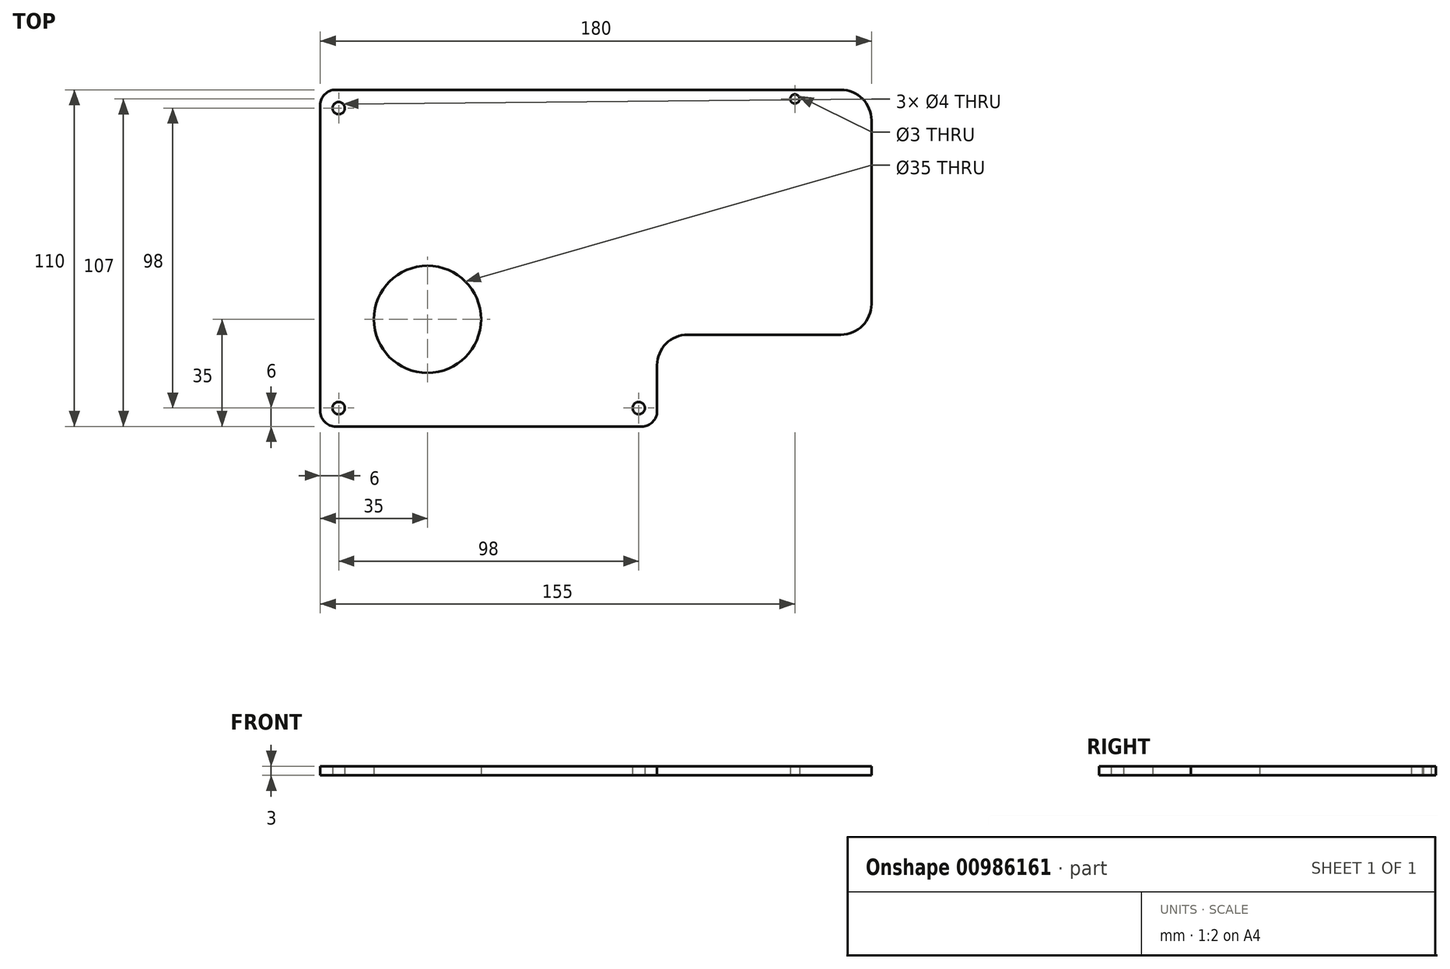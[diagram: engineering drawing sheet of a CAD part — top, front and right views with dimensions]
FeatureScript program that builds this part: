
annotation { "Feature Type Name" : "Feature", "Feature Type Description" : "" }
export const myFeature = defineFeature(function(context is Context, id is Id, definition is map)
    precondition{}
    {
        {
            var Q0;
            Q0=qCreatedBy(makeId("Top.planeOp"),FACE);
            var sketch = newSketch(context, id + "F0", { "sketchPlane" : qUnion([Q0])});
            skLineSegment(sketch, "E0.top", {"start": v(0, 110) * mm, "end": v(180, 110) * mm});
            skLineSegment(sketch, "E0.left", {"start": v(0, 0) * mm, "end": v(0, 110) * mm});
            skLineSegment(sketch, "E1", {"start": v(180, 110) * mm, "end": v(180, 30) * mm});
            skLineSegment(sketch, "E2", {"start": v(180, 30) * mm, "end": v(110, 30) * mm});
            skLineSegment(sketch, "E3", {"start": v(110, 30) * mm, "end": v(110, 0) * mm});
            skLineSegment(sketch, "E4", {"start": v(110, 0) * mm, "end": v(0, 0) * mm});
            skCircle(sketch, "E5", {"center": v(6, 104) * mm, "radius": 2 * mm});
            skCircle(sketch, "E6", {"center": v(6, 6) * mm, "radius": 2 * mm});
            skCircle(sketch, "E7", {"center": v(104, 6) * mm, "radius": 2 * mm});
            skCircle(sketch, "E8", {"center": v(155, 107) * mm, "radius": 1.5 * mm});
            skCircle(sketch, "E9", {"center": v(35, 35) * mm, "radius": 17.5 * mm});
            skSolve(sketch);
        }
        {
            var Q0;
            Q0=makeQuery(id+"F0.imprint","IMPRINT",FACE,{"disambiguationData":[TD([[makeQuery(id+"F0.imprint","IMPRINT",EDGE,{"derivedFrom":sQuery(id+"F0.wireOp",EDGE,"E0.top")}),-1.0]])]});
            extrude(context, id + "F1", {"entities" : qUnion([Q0]), "depth" : 3 * mm, "offsetDistance" : 25 * mm});
        }
        {
            var Q0;
            Q0=makeQuery(id+"F1.opExtrude","SWEPT_EDGE",EDGE,{"disambiguationData":[OSD([sQuery(id+"F0.wireOp",EDGE,"E2"),sQuery(id+"F0.wireOp",EDGE,"E3")])]});
            var Q1;
            Q1=makeQuery(id+"F1.opExtrude","SWEPT_EDGE",EDGE,{"disambiguationData":[OSD([sQuery(id+"F0.wireOp",EDGE,"E1"),sQuery(id+"F0.wireOp",EDGE,"E2")])]});
            var Q2;
            Q2=makeQuery(id+"F1.opExtrude","SWEPT_EDGE",EDGE,{"disambiguationData":[OSD([sQuery(id+"F0.wireOp",EDGE,"E0.top"),sQuery(id+"F0.wireOp",EDGE,"E1")])]});
            fillet(context, id + "F2", {"entities" : qUnion([Q0, Q1, Q2]), "radius" : 10 * mm, "tangentPropagation" : true, "allowEdgeOverflow" : false});
        }
        {
            var Q0;
            Q0=makeQuery(id+"F1.opExtrude","SWEPT_EDGE",EDGE,{"disambiguationData":[OSD([sQuery(id+"F0.wireOp",EDGE,"E3"),sQuery(id+"F0.wireOp",EDGE,"E4")])]});
            var Q1;
            Q1=makeQuery(id+"F1.opExtrude","SWEPT_EDGE",EDGE,{"disambiguationData":[OSD([sQuery(id+"F0.wireOp",EDGE,"E0.left"),sQuery(id+"F0.wireOp",EDGE,"E4")])]});
            var Q2;
            Q2=makeQuery(id+"F1.opExtrude","SWEPT_EDGE",EDGE,{"disambiguationData":[OSD([sQuery(id+"F0.wireOp",EDGE,"E0.top"),sQuery(id+"F0.wireOp",EDGE,"E0.left")])]});
            fillet(context, id + "F3", {"entities" : qUnion([Q0, Q1, Q2]), "radius" : 5 * mm, "tangentPropagation" : true, "allowEdgeOverflow" : false});
        }
    });
